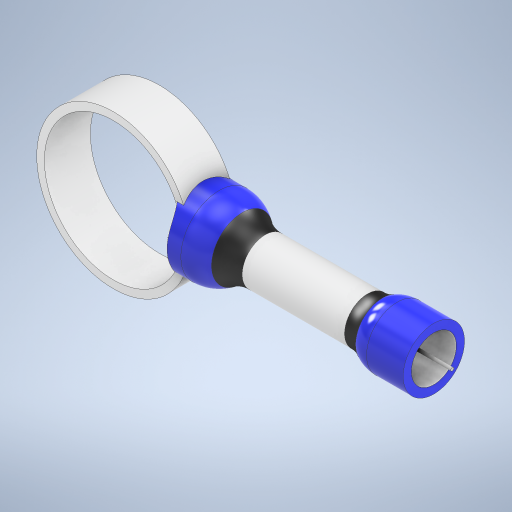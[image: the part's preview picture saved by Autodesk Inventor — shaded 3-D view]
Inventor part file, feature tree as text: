
AUTODESK INVENTOR PART (.ipt)
format: ipt  version: 2024 (Build 280153000, 153)  size: 550,912 bytes
history: native  units: mm
features: extrude x5, fillet x4, sketch x3, revolve x1, mirror x1, shell x1
ambient origin geometry x8: Origin, YZ Plane, XZ Plane, XY Plane, X Axis, Y Axis, Z Axis, Center Point
bodies: Solid1 (feature_tree)
feature tree (15):
  sketch  "Sketch1"  dims[d0=90.0mm d1=100.0mm]
  extrude  "Extrusion1"  Depth=100.0mm
  revolve  "Revolution1"  [1 undecoded]
  fillet  "Fillet1"  Radius=100.0mm
  fillet  "Fillet2"  Radius=15.0mm
  fillet  "Fillet3"  Radius=15.0mm
  mirror  "Mirror1"
  shell  "Shell1"  Thickness=15.0mm
  sketch  "Sketch2"  dims[d2=25.0mm d3=25.0mm d4=100.0mm d5=15.0mm d6=15.0mm d7=15.0mm d8=0.0mm]
  extrude  "Extrusion2"  Depth=25.0mm
  fillet  "Fillet4"  Radius=10.0mm
  extrude  "Extrusion3"  Depth=1.0mm
  extrude  "Extrusion4"  Depth=40.0mm
  extrude  "Extrusion5"  Depth=30.0mm TaperAngle=0.0deg
  sketch  "Sketch3"  dims[d9=180.0deg d10=25.0mm d11=10.0mm d12=1.0mm d13=5.0mm d14=30.0mm d15=0.0mm d16=20.0mm d17=30.0mm d18=0.0mm d19=2.0mm d20=0.0mm d21=2.0mm d22=40.0mm d23=0.0mm]
note: 1 required parameter value undecoded (feature->parameter linkage not recoverable at this tier; creation-order binding heuristic only, values carry confidence <= 0.55)
